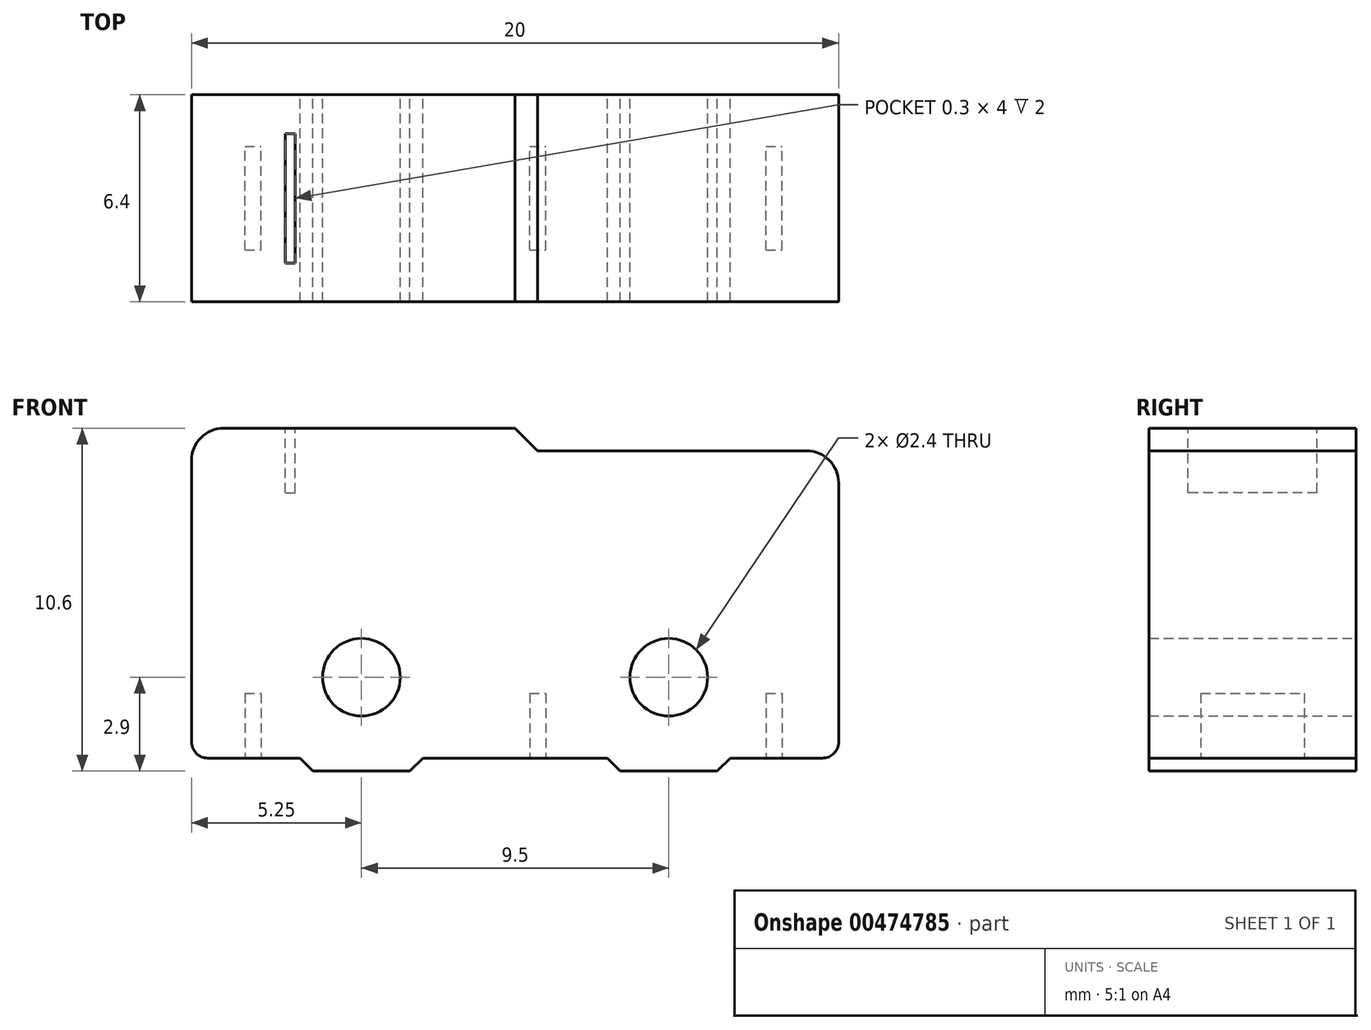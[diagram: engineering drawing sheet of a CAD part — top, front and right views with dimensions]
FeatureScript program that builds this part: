
annotation { "Feature Type Name" : "Feature", "Feature Type Description" : "" }
export const myFeature = defineFeature(function(context is Context, id is Id, definition is map)
    precondition{}
    {
        {
            var Q0;
            Q0=qCreatedBy(makeId("Front.planeOp"),FACE);
            var sketch = newSketch(context, id + "F0", { "sketchPlane" : qUnion([Q0])});
            skLineSegment(sketch, "E0.bottom", {"start": v(0.5, 0) * mm, "end": v(3.35, 0) * mm});
            skLineSegment(sketch, "E0.top", {"start": v(1, 10.2) * mm, "end": v(10, 10.2) * mm});
            skLineSegment(sketch, "E0.left", {"start": v(0, 0.5) * mm, "end": v(0, 9.2) * mm});
            skLineSegment(sketch, "E0.right", {"start": v(20, 0.5) * mm, "end": v(20, 8.5) * mm});
            skLineSegment(sketch, "E1", {"start": v(10, 10.2) * mm, "end": v(10.7, 9.5) * mm});
            skLineSegment(sketch, "E2", {"start": v(10.7, 9.5) * mm, "end": v(19, 9.5) * mm});
            skLineSegment(sketch, "E3", {"start": v(3.35, 0) * mm, "end": v(3.75, -0.4) * mm});
            skLineSegment(sketch, "E4", {"start": v(3.75, -0.4) * mm, "end": v(6.75, -0.4) * mm});
            skLineSegment(sketch, "E5", {"start": v(6.75, -0.4) * mm, "end": v(7.15, 0) * mm});
            skLineSegment(sketch, "E6", {"start": v(12.85, 0) * mm, "end": v(13.25, -0.4) * mm});
            skLineSegment(sketch, "E7", {"start": v(13.25, -0.4) * mm, "end": v(16.25, -0.4) * mm});
            skLineSegment(sketch, "E8", {"start": v(16.25, -0.4) * mm, "end": v(16.65, 0) * mm});
            skLineSegment(sketch, "E9.trimOffspring", {"start": v(7.15, 0) * mm, "end": v(12.85, 0) * mm});
            skLineSegment(sketch, "E10.trimOffspring", {"start": v(16.65, 0) * mm, "end": v(19.5, 0) * mm});
            skCircle(sketch, "E11", {"center": v(5.25, 2.5) * mm, "radius": 1.2 * mm});
            skCircle(sketch, "E12", {"center": v(14.75, 2.5) * mm, "radius": 1.2 * mm});
            skLineSegment(sketch, "E13", {"start": v(5.25, 2.5) * mm, "end": v(14.75, 2.5) * mm, "construction": true});
            skLineSegment(sketch, "E14", {"start": v(5.25, 2.5) * mm, "end": v(5.25, -0.4) * mm, "construction": true});
            skLineSegment(sketch, "E15", {"start": v(14.75, 2.5) * mm, "end": v(14.75, -0.4) * mm, "construction": true});
            skPoint(sketch, "E16.visualSharp", {"position": v(0, 10.2) * mm});
            skArc(sketch, "E16.filletArc", {"start": v(1, 10.2) * mm, "mid": v(0.3, 9.9) * mm, "end": v(0, 9.2) * mm});
            skPoint(sketch, "E17.visualSharp", {"position": v(20, 9.5) * mm});
            skArc(sketch, "E17.filletArc", {"start": v(20, 8.5) * mm, "mid": v(19.7, 9.2) * mm, "end": v(19, 9.5) * mm});
            skPoint(sketch, "E18.visualSharp", {"position": v(0, 0) * mm});
            skArc(sketch, "E18.filletArc", {"start": v(0, 0.5) * mm, "mid": v(0.15, 0.15) * mm, "end": v(0.5, 0) * mm});
            skPoint(sketch, "E19.visualSharp", {"position": v(20, 0) * mm});
            skArc(sketch, "E19.filletArc", {"start": v(19.5, 0) * mm, "mid": v(19.85, 0.15) * mm, "end": v(20, 0.5) * mm});
            skSolve(sketch);
        }
        {
            var Q0;
            Q0=qSketchRegion(id+"F0",true);
            extrude(context, id + "F1", {"entities" : qUnion([Q0]), "depth" : 6.4 * mm, "offsetDistance" : 25 * mm});
        }
        {
            var Q0;
            Q0=makeQuery(id+"F1.opExtrude","SWEPT_FACE",FACE,{"disambiguationData":[OSD([sQuery(id+"F0.wireOp",EDGE,"E0.bottom")])]});
            var sketch = newSketch(context, id + "F2", { "sketchPlane" : qUnion([Q0])});
            skLineSegment(sketch, "E20", {"start": v(0.5, 3.2) * mm, "end": v(19.5, 3.2) * mm, "construction": true});
            skLineSegment(sketch, "E21.bottom", {"start": v(1.65, 4.8) * mm, "end": v(2.15, 4.8) * mm});
            skLineSegment(sketch, "E21.top", {"start": v(1.65, 1.6) * mm, "end": v(2.15, 1.6) * mm});
            skLineSegment(sketch, "E21.left", {"start": v(1.65, 4.8) * mm, "end": v(1.65, 1.6) * mm});
            skLineSegment(sketch, "E21.right", {"start": v(2.15, 4.8) * mm, "end": v(2.15, 1.6) * mm});
            skLineSegment(sketch, "E22.bottom", {"start": v(10.45, 4.8) * mm, "end": v(10.95, 4.8) * mm});
            skLineSegment(sketch, "E22.top", {"start": v(10.45, 1.6) * mm, "end": v(10.95, 1.6) * mm});
            skLineSegment(sketch, "E22.left", {"start": v(10.45, 4.8) * mm, "end": v(10.45, 1.6) * mm});
            skLineSegment(sketch, "E22.right", {"start": v(10.95, 4.8) * mm, "end": v(10.95, 1.6) * mm});
            skLineSegment(sketch, "E23.bottom", {"start": v(17.75, 4.8) * mm, "end": v(18.25, 4.8) * mm});
            skLineSegment(sketch, "E23.top", {"start": v(17.75, 1.6) * mm, "end": v(18.25, 1.6) * mm});
            skLineSegment(sketch, "E23.left", {"start": v(17.75, 4.8) * mm, "end": v(17.75, 1.6) * mm});
            skLineSegment(sketch, "E23.right", {"start": v(18.25, 4.8) * mm, "end": v(18.25, 1.6) * mm});
            skLineSegment(sketch, "E24", {"start": v(1.9, 4.8) * mm, "end": v(1.9, 1.6) * mm, "construction": true});
            skLineSegment(sketch, "E25", {"start": v(10.7, 4.8) * mm, "end": v(10.7, 1.6) * mm, "construction": true});
            skLineSegment(sketch, "E26", {"start": v(18, 4.8) * mm, "end": v(18, 1.6) * mm, "construction": true});
            skSolve(sketch);
        }
        {
            var Q0;
            Q0=qSketchRegion(id+"F2",true);
            extrude(context, id + "F3", {"entities" : qUnion([Q0]), "operationType" : NewBodyOperationType.REMOVE, "oppositeDirection" : true, "depth" : 2 * mm, "offsetDistance" : 25 * mm});
        }
        {
            var Q0;
            Q0=makeQuery(id+"F1.opExtrude","SWEPT_FACE",FACE,{"disambiguationData":[OSD([sQuery(id+"F0.wireOp",EDGE,"E0.top")])]});
            var sketch = newSketch(context, id + "F4", { "sketchPlane" : qUnion([Q0])});
            skLineSegment(sketch, "E27", {"start": v(1, -3.2) * mm, "end": v(10, -3.2) * mm, "construction": true});
            skLineSegment(sketch, "E28.bottom", {"start": v(2.9, -1.2) * mm, "end": v(3.2, -1.2) * mm});
            skLineSegment(sketch, "E28.top", {"start": v(2.9, -5.2) * mm, "end": v(3.2, -5.2) * mm});
            skLineSegment(sketch, "E28.left", {"start": v(3.2, -1.2) * mm, "end": v(3.2, -5.2) * mm});
            skLineSegment(sketch, "E28.right", {"start": v(2.9, -1.2) * mm, "end": v(2.9, -5.2) * mm});
            skLineSegment(sketch, "E29", {"start": v(3.05, -1.2) * mm, "end": v(3.05, -5.2) * mm, "construction": true});
            skSolve(sketch);
        }
        {
            var Q0;
            Q0=qSketchRegion(id+"F4",true);
            extrude(context, id + "F5", {"entities" : qUnion([Q0]), "operationType" : NewBodyOperationType.REMOVE, "oppositeDirection" : true, "depth" : 2 * mm, "offsetDistance" : 25 * mm});
        }
    });
